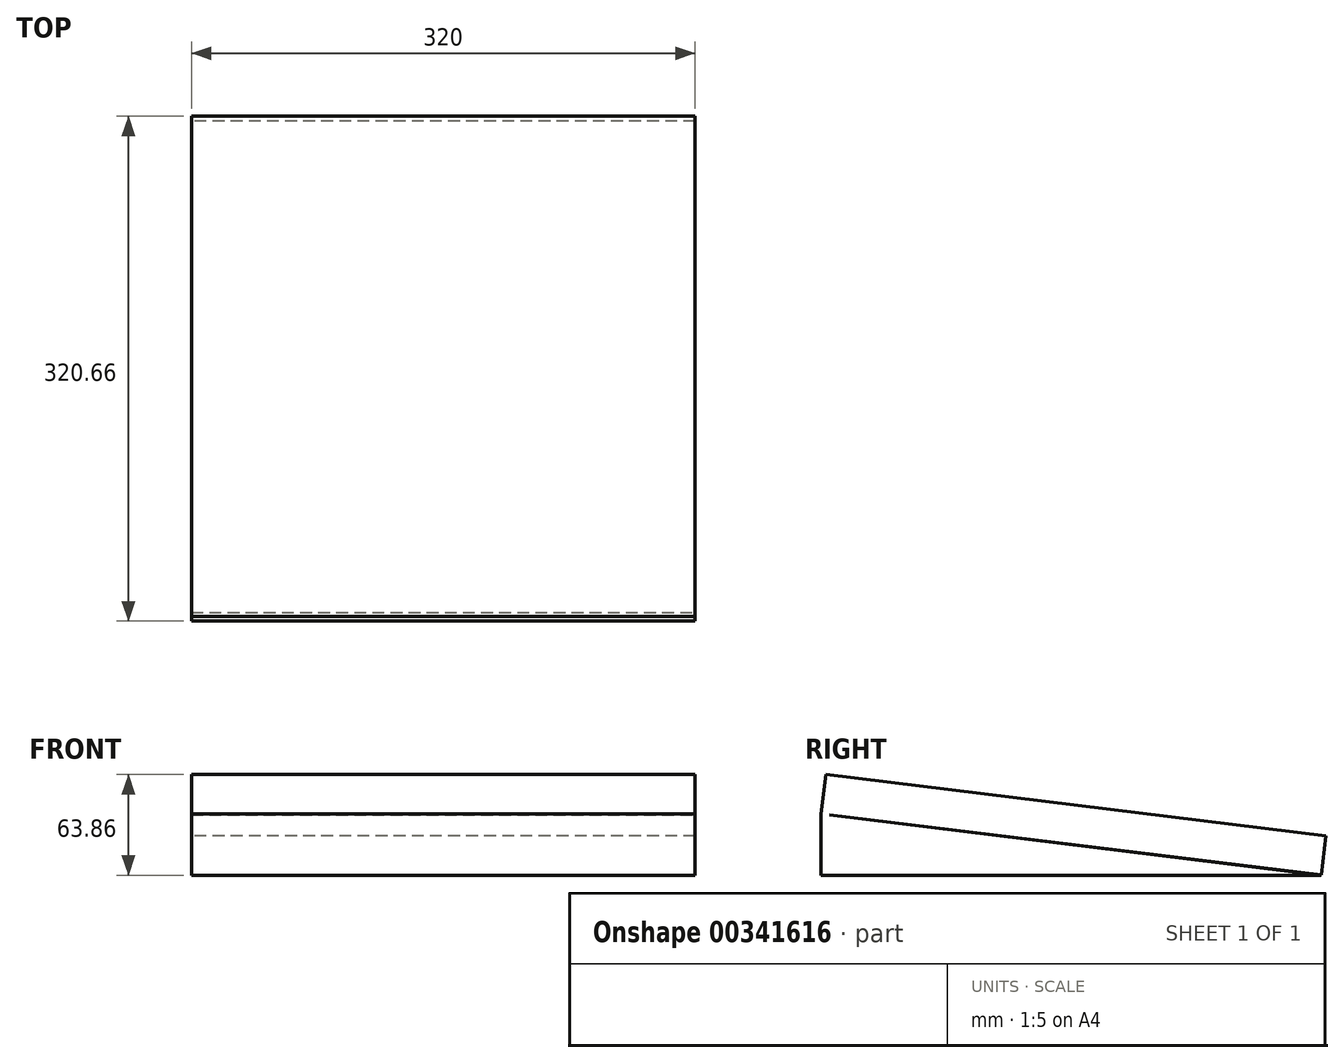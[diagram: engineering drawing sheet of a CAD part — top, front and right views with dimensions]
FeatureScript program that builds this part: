
annotation { "Feature Type Name" : "Feature", "Feature Type Description" : "" }
export const myFeature = defineFeature(function(context is Context, id is Id, definition is map)
    precondition{}
    {
        {
            var Q0;
            Q0=qCreatedBy(makeId("Top.planeOp"),FACE);
            var sketch = newSketch(context, id + "F0", { "sketchPlane" : qUnion([Q0])});
            skLineSegment(sketch, "E0.bottom", {"start": v(160, -160) * mm, "end": v(-160, -160) * mm});
            skLineSegment(sketch, "E0.top", {"start": v(160, 160) * mm, "end": v(-160, 160) * mm});
            skLineSegment(sketch, "E0.left", {"start": v(160, -160) * mm, "end": v(160, 160) * mm});
            skLineSegment(sketch, "E0.right", {"start": v(-160, -160) * mm, "end": v(-160, 160) * mm});
            skPoint(sketch, "E0.middle", {"position": v(0, 0) * mm});
            skSolve(sketch);
        }
        {
            var Q0;
            Q0=makeQuery(id+"F0.imprint","IMPRINT",FACE,{"disambiguationData":[TD([[makeQuery(id+"F0.imprint","IMPRINT",EDGE,{"derivedFrom":sQuery(id+"F0.wireOp",EDGE,"E0.bottom")}),-1.0]])]});
            extrude(context, id + "F1", {"entities" : qUnion([Q0]), "depth" : 25 * mm});
        }
        {
            var Q0;
            Q0=makeQuery(id+"F1.opExtrude","SWEPT_BODY",BODY,{"disambiguationData":[OSD([sQuery(id+"F0.wireOp",EDGE,"E0.bottom"),sQuery(id+"F0.wireOp",EDGE,"E0.top"),sQuery(id+"F0.wireOp",EDGE,"E0.left"),sQuery(id+"F0.wireOp",EDGE,"E0.right")])]});
            var Q1;
            Q1=qCreatedBy(makeId("Origin.pointOp"),VERTEX);
            var Q2;
            Q2=makeQuery(id+"F1.opExtrude","CAP_EDGE",EDGE,{"disambiguationData":[OSD([sQuery(id+"F0.wireOp",EDGE,"E0.bottom")])],"isStart":true});
            transform(context, id + "F2", {"entities" : qUnion([Q0]), "transformType" : TransformType.ROTATION, "transformAxis" : qUnion([Q2]), "angle" : 7 * degree, "makeCopy" : false});
        }
        {
            var Q0;
            Q0=qCreatedBy(makeId("Right.planeOp"),FACE);
            var sketch = newSketch(context, id + "F3", { "sketchPlane" : qUnion([Q0])});
            skLineSegment(sketch, "E1.bottom", {"start": v(-160, 0) * mm, "end": v(157.52, 0) * mm});
            skLineSegment(sketch, "E1.top", {"start": v(-160, -39.05) * mm, "end": v(157.52, -39.05) * mm});
            skLineSegment(sketch, "E1.left", {"start": v(-160, 0) * mm, "end": v(-160, -39.05) * mm});
            skLineSegment(sketch, "E1.right", {"start": v(157.52, 0) * mm, "end": v(157.52, -39.05) * mm});
            skLineSegment(sketch, "E2", {"start": v(157.52, -39.05) * mm, "end": v(-160, 0) * mm});
            skSolve(sketch);
        }
        {
            var Q0;
            Q0=makeQuery(id+"F3.imprint","IMPRINT",FACE,{"disambiguationData":[TD([[makeQuery(id+"F3.imprint","IMPRINT",EDGE,{"derivedFrom":sQuery(id+"F3.wireOp",EDGE,"E1.top")}),1.0]])]});
            extrude(context, id + "F4", {"entities" : qUnion([Q0]), "operationType" : NewBodyOperationType.ADD, "endBound" : BoundingType.SYMMETRIC, "depth" : 320 * mm});
        }
    });
